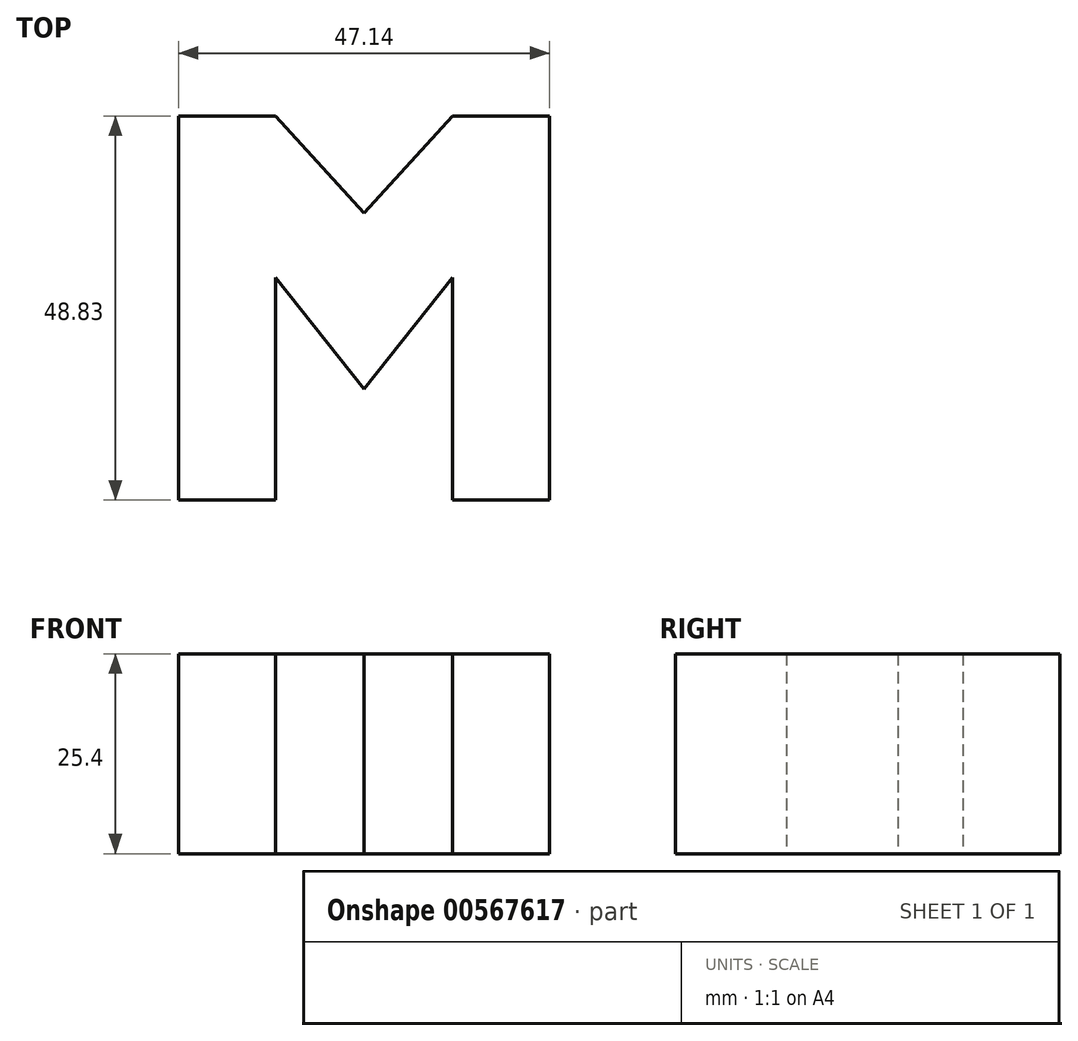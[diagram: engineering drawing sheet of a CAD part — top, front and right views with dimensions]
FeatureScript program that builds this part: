
annotation { "Feature Type Name" : "Feature", "Feature Type Description" : "" }
export const myFeature = defineFeature(function(context is Context, id is Id, definition is map)
    precondition{}
    {
        {
            var Q0;
            Q0=qCreatedBy(makeId("Top.planeOp"),FACE);
            var sketch = newSketch(context, id + "F0", { "sketchPlane" : qUnion([Q0])});
            skLineSegment(sketch, "E0", {"start": v(-23.57, 0) * mm, "end": v(-23.57, 48.83) * mm});
            skLineSegment(sketch, "E1", {"start": v(-23.57, 48.83) * mm, "end": v(-11.22, 48.83) * mm});
            skLineSegment(sketch, "E2", {"start": v(-11.22, 48.83) * mm, "end": v(0, 36.49) * mm});
            skLineSegment(sketch, "E3", {"start": v(-23.57, 0) * mm, "end": v(-11.22, 0) * mm});
            skLineSegment(sketch, "E4", {"start": v(-11.22, 28.26) * mm, "end": v(-11.22, 0) * mm});
            skLineSegment(sketch, "E5", {"start": v(-11.22, 28.26) * mm, "end": v(0, 14.13) * mm});
            skPoint(sketch, "E5.endSnap0", {"position": v(-11.22, 14.13) * mm});
            skLineSegment(sketch, "E6.MirrorCS", {"start": v(23.57, 0) * mm, "end": v(23.57, 48.83) * mm});
            skLineSegment(sketch, "E7.MirrorCS", {"start": v(23.57, 48.83) * mm, "end": v(11.22, 48.83) * mm});
            skLineSegment(sketch, "E8.MirrorCS", {"start": v(11.22, 48.83) * mm, "end": v(0, 36.49) * mm});
            skLineSegment(sketch, "E9.MirrorCS", {"start": v(11.22, 28.26) * mm, "end": v(0, 14.13) * mm});
            skLineSegment(sketch, "E10.MirrorCS", {"start": v(11.22, 28.26) * mm, "end": v(11.22, 0) * mm});
            skLineSegment(sketch, "E11.MirrorCS", {"start": v(23.57, 0) * mm, "end": v(11.22, 0) * mm});
            skSolve(sketch);
        }
        {
            var Q0;
            Q0 = qSketchRegion(id + "F0", true);
            extrude(context, id + "F1", {"entities" : qUnion([Q0]), "depth" : 25.4 * mm, "offsetDistance" : 25.4 * mm});
        }
    });
